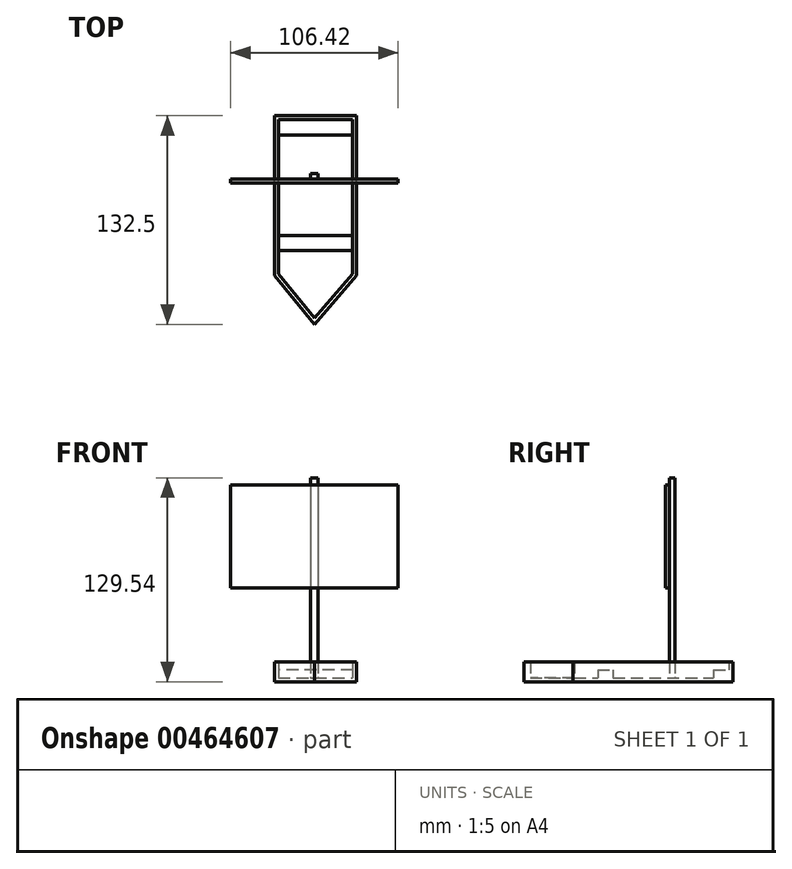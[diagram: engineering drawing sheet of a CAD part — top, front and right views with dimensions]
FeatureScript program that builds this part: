
annotation { "Feature Type Name" : "Feature", "Feature Type Description" : "" }
export const myFeature = defineFeature(function(context is Context, id is Id, definition is map)
    precondition{}
    {
        {
            var Q0;
            Q0=qCreatedBy(makeId("Top.planeOp"),FACE);
            var sketch = newSketch(context, id + "F0", { "sketchPlane" : qUnion([Q0])});
            skLineSegment(sketch, "E0.bottom", {"start": v(0, 0) * mm, "end": v(-25.54, 0) * mm});
            skLineSegment(sketch, "E0.top", {"start": v(0, 76.04) * mm, "end": v(-25.54, 76.04) * mm});
            skLineSegment(sketch, "E0.left", {"start": v(0, 0) * mm, "end": v(0, 76.04) * mm});
            skLineSegment(sketch, "E0.right", {"start": v(-25.54, 0) * mm, "end": v(-25.54, 76.04) * mm});
            skLineSegment(sketch, "E1.bottom", {"start": v(0, 0) * mm, "end": v(26.67, 0) * mm});
            skLineSegment(sketch, "E1.top", {"start": v(0, 76.04) * mm, "end": v(26.67, 76.04) * mm});
            skLineSegment(sketch, "E1.right", {"start": v(26.67, 0) * mm, "end": v(26.67, 76.04) * mm});
            skLineSegment(sketch, "E2.top", {"start": v(0, -25.54) * mm, "end": v(26.67, -25.54) * mm});
            skLineSegment(sketch, "E2.left", {"start": v(0, 0) * mm, "end": v(0, -25.54) * mm});
            skLineSegment(sketch, "E2.right", {"start": v(26.67, 0) * mm, "end": v(26.67, -25.54) * mm});
            skLineSegment(sketch, "E3.bottom", {"start": v(0, -25.54) * mm, "end": v(-25.54, -25.54) * mm});
            skLineSegment(sketch, "E3.left", {"start": v(0, -25.54) * mm, "end": v(0, 0) * mm});
            skLineSegment(sketch, "E3.right", {"start": v(-25.54, -25.54) * mm, "end": v(-25.54, 0) * mm});
            skLineSegment(sketch, "E4", {"start": v(-25.54, -25.54) * mm, "end": v(0, -56.46) * mm});
            skLineSegment(sketch, "E5", {"start": v(0, -56.46) * mm, "end": v(26.67, -25.54) * mm});
            skSolve(sketch);
        }
        {
            var Q0;
            Q0 = qSketchRegion(id + "F0", true);
            extrude(context, id + "F1", {"entities" : qUnion([Q0]), "depth" : 12.7 * mm});
        }
        {
            var Q0;
            Q0=makeQuery(id+"F1.opExtrude","CAP_FACE",FACE,{"disambiguationData":[OSD([sQuery(id+"F0.wireOp",EDGE,"E0.top"),sQuery(id+"F0.wireOp",EDGE,"E0.right"),sQuery(id+"F0.wireOp",EDGE,"E1.top"),sQuery(id+"F0.wireOp",EDGE,"E1.right"),sQuery(id+"F0.wireOp",EDGE,"E2.right"),sQuery(id+"F0.wireOp",EDGE,"E3.right"),sQuery(id+"F0.wireOp",EDGE,"E4"),sQuery(id+"F0.wireOp",EDGE,"E5")])],"isStart":false});
            shell(context, id + "F2", {"entities" : qUnion([Q0]), "thickness" : 2.54 * mm});
        }
        {
            var Q0;
            Q0=makeQuery(id+"F2.opShell","OFFSET_FACE",FACE,{"disambiguationData":[OSD([sQuery(id+"F0.wireOp",EDGE,"E0.top"),sQuery(id+"F0.wireOp",EDGE,"E0.right"),sQuery(id+"F0.wireOp",EDGE,"E1.top"),sQuery(id+"F0.wireOp",EDGE,"E1.right"),sQuery(id+"F0.wireOp",EDGE,"E2.right"),sQuery(id+"F0.wireOp",EDGE,"E3.right"),sQuery(id+"F0.wireOp",EDGE,"E4"),sQuery(id+"F0.wireOp",EDGE,"E5")])]});
            var sketch = newSketch(context, id + "F3", { "sketchPlane" : qUnion([Q0])});
            skLineSegment(sketch, "E6.bottom", {"start": v(-23, 73.5) * mm, "end": v(24.13, 73.5) * mm});
            skLineSegment(sketch, "E6.top", {"start": v(-23, 63.84) * mm, "end": v(24.13, 63.84) * mm});
            skLineSegment(sketch, "E6.left", {"start": v(-23, 73.5) * mm, "end": v(-23, 63.84) * mm});
            skLineSegment(sketch, "E6.right", {"start": v(24.13, 73.5) * mm, "end": v(24.13, 63.84) * mm});
            skLineSegment(sketch, "E7.bottom", {"start": v(-23, 0) * mm, "end": v(24.13, 0) * mm});
            skLineSegment(sketch, "E7.top", {"start": v(-23, -9.65) * mm, "end": v(24.13, -9.65) * mm});
            skLineSegment(sketch, "E7.left", {"start": v(-23, 0) * mm, "end": v(-23, -9.65) * mm});
            skLineSegment(sketch, "E7.right", {"start": v(24.13, 0) * mm, "end": v(24.13, -9.65) * mm});
            skSolve(sketch);
        }
        {
            var Q0;
            Q0 = qSketchRegion(id + "F3", true);
            extrude(context, id + "F4", {"entities" : qUnion([Q0]), "operationType" : NewBodyOperationType.ADD, "depth" : 5.08 * mm});
        }
        {
            var Q0;
            {var subQ0=sQuery(id+"F0.wireOp",EDGE,"E3.right");var subQ1=sQuery(id+"F0.wireOp",EDGE,"E0.right");var subQ2=sQuery(id+"F0.wireOp",EDGE,"E2.right");var subQ3=sQuery(id+"F0.wireOp",EDGE,"E1.right");Q0=makeQuery(id+"F4.boolean.opBoolean","SPLIT",FACE,{"disambiguationData":[TD([makeQuery(id+"F4.opExtrude","SWEPT_FACE",FACE,{"disambiguationData":[OSD([sQuery(id+"F3.wireOp",EDGE,"E6.top")])]})])],"derivedFrom":makeQuery(id+"F2.opShell","OFFSET_FACE",FACE,{"disambiguationData":[OSD([sQuery(id+"F0.wireOp",EDGE,"E0.top"),subQ1,sQuery(id+"F0.wireOp",EDGE,"E1.top"),subQ3,subQ2,subQ0,sQuery(id+"F0.wireOp",EDGE,"E4"),sQuery(id+"F0.wireOp",EDGE,"E5")])]})});}
            var sketch = newSketch(context, id + "F5", { "sketchPlane" : qUnion([Q0])});
            skLineSegment(sketch, "E8.bottom", {"start": v(-2.55, 35.75) * mm, "end": v(2.27, 35.75) * mm});
            skLineSegment(sketch, "E8.top", {"start": v(-2.55, 39.44) * mm, "end": v(2.27, 39.44) * mm});
            skLineSegment(sketch, "E8.left", {"start": v(-2.55, 35.75) * mm, "end": v(-2.55, 39.44) * mm});
            skLineSegment(sketch, "E8.right", {"start": v(2.27, 35.75) * mm, "end": v(2.27, 39.44) * mm});
            skSolve(sketch);
        }
        {
            var Q0;
            Q0 = qSketchRegion(id + "F5", true);
            extrude(context, id + "F6", {"entities" : qUnion([Q0]), "operationType" : NewBodyOperationType.ADD, "depth" : 127 * mm});
        }
        {
            var Q0;
            Q0=makeQuery(id+"F6.opExtrude","SWEPT_FACE",FACE,{"disambiguationData":[OSD([sQuery(id+"F5.wireOp",EDGE,"E8.bottom")])]});
            var sketch = newSketch(context, id + "F7", { "sketchPlane" : qUnion([Q0])});
            skLineSegment(sketch, "E9.bottom", {"start": v(-2.55, 59.75) * mm, "end": v(2.27, 59.75) * mm});
            skLineSegment(sketch, "E9.top", {"start": v(-2.55, 62.7) * mm, "end": v(2.27, 62.7) * mm});
            skLineSegment(sketch, "E9.left", {"start": v(-2.55, 59.75) * mm, "end": v(-2.55, 62.7) * mm});
            skLineSegment(sketch, "E9.right", {"start": v(2.27, 59.75) * mm, "end": v(2.27, 62.7) * mm});
            skSolve(sketch);
        }
        {
            var Q0;
            Q0 = qSketchRegion(id + "F7", true);
            extrude(context, id + "F8", {"entities" : qUnion([Q0]), "operationType" : NewBodyOperationType.ADD, "depth" : 2.54 * mm});
        }
        {
            var Q0;
            Q0=makeQuery(id+"F8.boolean.opBoolean","MERGE",FACE,{"derivedFrom":[makeQuery(id+"F6.opExtrude","SWEPT_FACE",FACE,{"disambiguationData":[OSD([sQuery(id+"F5.wireOp",EDGE,"E8.right")])]}),makeQuery(id+"F8.opExtrude","SWEPT_FACE",FACE,{"disambiguationData":[OSD([sQuery(id+"F7.wireOp",EDGE,"E9.right")])]})]});
            var sketch = newSketch(context, id + "F9", { "sketchPlane" : qUnion([Q0])});
            skLineSegment(sketch, "E10.bottom", {"start": v(33.2, 62.7) * mm, "end": v(35.75, 62.7) * mm});
            skLineSegment(sketch, "E10.top", {"start": v(33.2, 59.75) * mm, "end": v(35.75, 59.75) * mm});
            skLineSegment(sketch, "E10.left", {"start": v(33.2, 62.7) * mm, "end": v(33.2, 59.75) * mm});
            skLineSegment(sketch, "E10.right", {"start": v(35.75, 62.7) * mm, "end": v(35.75, 59.75) * mm});
            skSolve(sketch);
        }
        {
            var Q0;
            Q0=makeQuery(id+"F9.imprint","IMPRINT",FACE,{"disambiguationData":[TD([[makeQuery(id+"F9.imprint","IMPRINT",EDGE,{"derivedFrom":sQuery(id+"F9.wireOp",EDGE,"E10.bottom")}),-1.0]])]});
            extrude(context, id + "F10", {"entities" : qUnion([Q0]), "operationType" : NewBodyOperationType.ADD, "depth" : 50.8 * mm});
        }
        {
            var Q0;
            Q0=makeQuery(id+"F8.boolean.opBoolean","MERGE",FACE,{"derivedFrom":[makeQuery(id+"F6.opExtrude","SWEPT_FACE",FACE,{"disambiguationData":[OSD([sQuery(id+"F5.wireOp",EDGE,"E8.left")])]}),makeQuery(id+"F8.opExtrude","SWEPT_FACE",FACE,{"disambiguationData":[OSD([sQuery(id+"F7.wireOp",EDGE,"E9.left")])]})]});
            var sketch = newSketch(context, id + "F11", { "sketchPlane" : qUnion([Q0])});
            skLineSegment(sketch, "E11.bottom", {"start": v(-35.75, 62.7) * mm, "end": v(-33.2, 62.7) * mm});
            skLineSegment(sketch, "E11.top", {"start": v(-35.75, 59.75) * mm, "end": v(-33.2, 59.75) * mm});
            skLineSegment(sketch, "E11.left", {"start": v(-35.75, 62.7) * mm, "end": v(-35.75, 59.75) * mm});
            skLineSegment(sketch, "E11.right", {"start": v(-33.2, 62.7) * mm, "end": v(-33.2, 59.75) * mm});
            skSolve(sketch);
        }
        {
            var Q0;
            Q0 = qSketchRegion(id + "F11", true);
            extrude(context, id + "F12", {"entities" : qUnion([Q0]), "operationType" : NewBodyOperationType.ADD, "depth" : 50.8 * mm});
        }
        {
            var Q0;
            Q0=makeQuery(id+"F12.boolean.opBoolean","MERGE",FACE,{"derivedFrom":[makeQuery(id+"F10.boolean.opBoolean","MERGE",FACE,{"derivedFrom":[makeQuery(id+"F8.opExtrude","SWEPT_FACE",FACE,{"disambiguationData":[OSD([sQuery(id+"F7.wireOp",EDGE,"E9.top")])]}),makeQuery(id+"F10.opExtrude","SWEPT_FACE",FACE,{"disambiguationData":[OSD([sQuery(id+"F9.wireOp",EDGE,"E10.bottom")])]})]}),makeQuery(id+"F12.opExtrude","SWEPT_FACE",FACE,{"disambiguationData":[OSD([sQuery(id+"F11.wireOp",EDGE,"E11.bottom")])]})]});
            var sketch = newSketch(context, id + "F13", { "sketchPlane" : qUnion([Q0])});
            skLineSegment(sketch, "E12.bottom", {"start": v(-53.35, 35.75) * mm, "end": v(53.07, 35.75) * mm});
            skLineSegment(sketch, "E12.top", {"start": v(-53.35, 33.2) * mm, "end": v(53.07, 33.2) * mm});
            skLineSegment(sketch, "E12.left", {"start": v(-53.35, 35.75) * mm, "end": v(-53.35, 33.2) * mm});
            skLineSegment(sketch, "E12.right", {"start": v(53.07, 35.75) * mm, "end": v(53.07, 33.2) * mm});
            skSolve(sketch);
        }
        {
            var Q0;
            Q0 = qSketchRegion(id + "F13", true);
            extrude(context, id + "F14", {"entities" : qUnion([Q0]), "operationType" : NewBodyOperationType.ADD, "depth" : 62.23 * mm});
        }
    });
